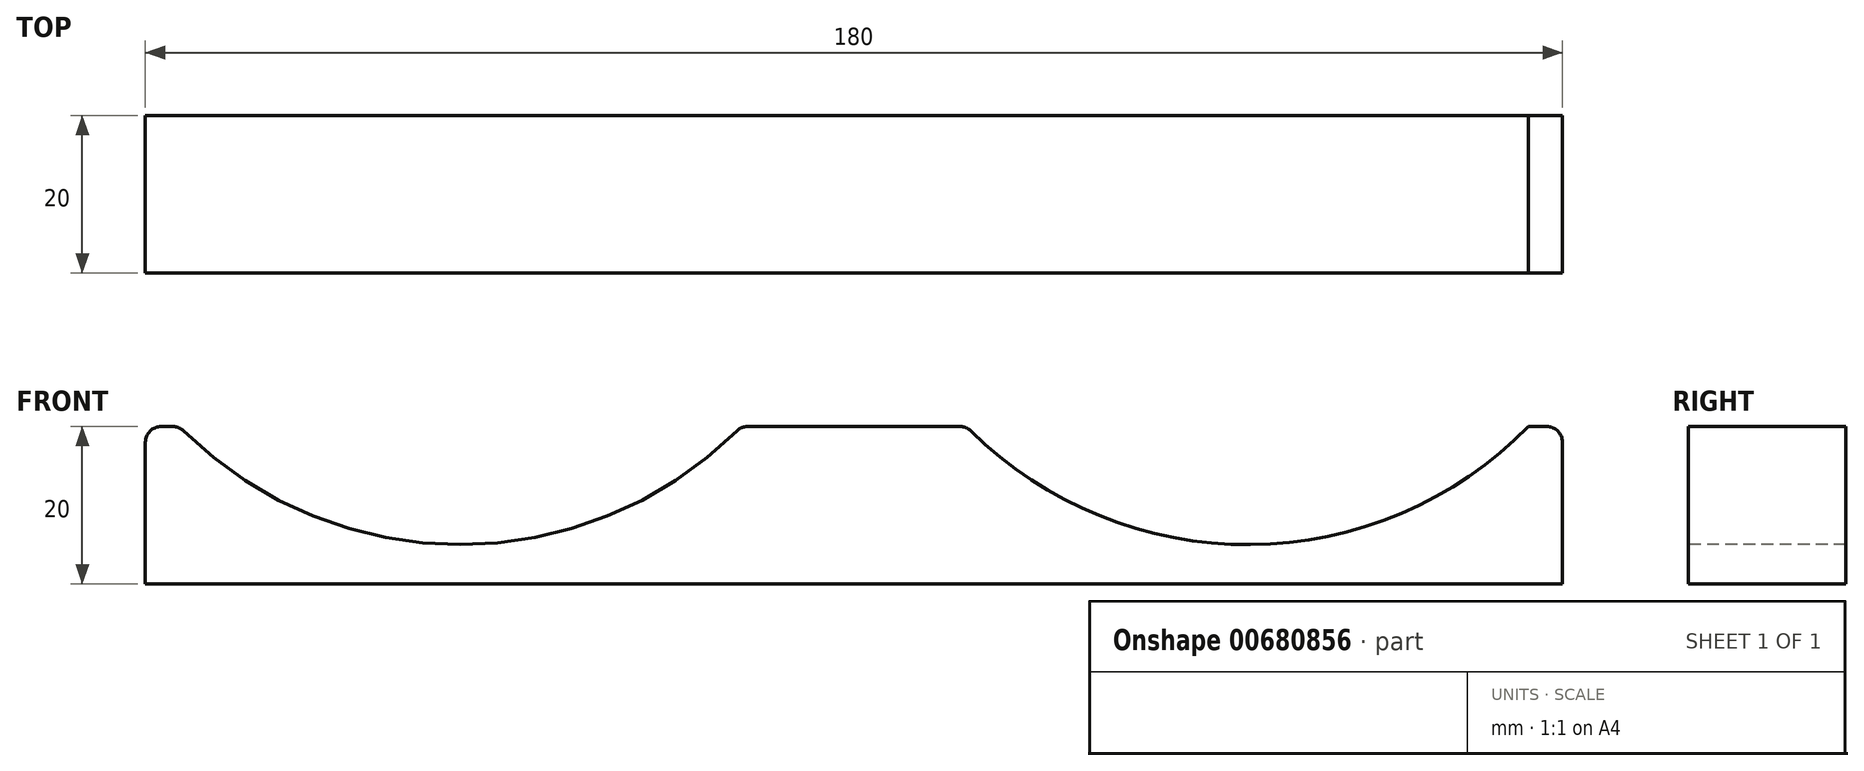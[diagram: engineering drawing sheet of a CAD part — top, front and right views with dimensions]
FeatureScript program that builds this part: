
annotation { "Feature Type Name" : "Feature", "Feature Type Description" : "" }
export const myFeature = defineFeature(function(context is Context, id is Id, definition is map)
    precondition{}
    {
        {
            var Q0;
            Q0=qCreatedBy(makeId("Front.planeOp"),FACE);
            var sketch = newSketch(context, id + "F0", { "sketchPlane" : qUnion([Q0])});
            skLineSegment(sketch, "E0.bottom", {"start": v(0, 0) * mm, "end": v(180, 0) * mm});
            skLineSegment(sketch, "E0.top", {"start": v(0, 20) * mm, "end": v(180, 20) * mm});
            skLineSegment(sketch, "E0.left", {"start": v(0, 0) * mm, "end": v(0, 20) * mm});
            skLineSegment(sketch, "E0.right", {"start": v(180, 0) * mm, "end": v(180, 20) * mm});
            skSolve(sketch);
        }
        {
            var Q0;
            Q0 = qSketchRegion(id + "F0", true);
            extrude(context, id + "F1", {"entities" : qUnion([Q0]), "oppositeDirection" : true, "depth" : 20 * mm, "offsetDistance" : 25 * mm});
        }
        {
            var Q0;
            Q0=makeQuery(id+"F1.opExtrude","CAP_FACE",FACE,{"disambiguationData":[OSD([sQuery(id+"F0.wireOp",EDGE,"E0.bottom"),sQuery(id+"F0.wireOp",EDGE,"E0.top"),sQuery(id+"F0.wireOp",EDGE,"E0.left"),sQuery(id+"F0.wireOp",EDGE,"E0.right")])],"isStart":true});
            var sketch = newSketch(context, id + "F2", { "sketchPlane" : qUnion([Q0])});
            skLineSegment(sketch, "E1", {"start": v(0, 0) * mm, "end": v(40, 0) * mm, "construction": true});
            skLineSegment(sketch, "E2", {"start": v(40, 0) * mm, "end": v(40, 55) * mm, "construction": true});
            skCircle(sketch, "E3", {"center": v(40, 55) * mm, "radius": 50 * mm});
            skLineSegment(sketch, "E4", {"start": v(40, 55) * mm, "end": v(140, 55) * mm, "construction": true});
            skCircle(sketch, "E5", {"center": v(140, 55) * mm, "radius": 50 * mm});
            skSolve(sketch);
        }
        {
            var Q0;
            {var subQ0=sQuery(id+"F2.wireOp",EDGE,"E3");var subQ1=makeQuery(id+"F1.opExtrude","CAP_EDGE",EDGE,{"disambiguationData":[OSD([sQuery(id+"F0.wireOp",EDGE,"E0.top")])],"isStart":true});var subQ2=makeQuery(id+"F2.imprint","INTERSECT",VERTEX,{"disambiguationData":[OD(0.0)],"derivedFrom":[subQ1,subQ0]});Q0=makeQuery(id+"F2.imprint","IMPRINT",FACE,{"disambiguationData":[TD([[makeQuery(id+"F2.imprint","IMPRINT",EDGE,{"disambiguationData":[TD([[subQ2,-1.0]])],"derivedFrom":subQ0}),1.0]])]});}
            var Q1;
            {var subQ0=sQuery(id+"F2.wireOp",EDGE,"E5");var subQ1=makeQuery(id+"F1.opExtrude","CAP_EDGE",EDGE,{"disambiguationData":[OSD([sQuery(id+"F0.wireOp",EDGE,"E0.top")])],"isStart":true});var subQ2=makeQuery(id+"F2.imprint","INTERSECT",VERTEX,{"disambiguationData":[OD(0.0)],"derivedFrom":[subQ1,subQ0]});Q1=makeQuery(id+"F2.imprint","IMPRINT",FACE,{"disambiguationData":[TD([[makeQuery(id+"F2.imprint","IMPRINT",EDGE,{"disambiguationData":[TD([[subQ2,1.0]])],"derivedFrom":subQ0}),1.0]])]});}
            extrude(context, id + "F3", {"entities" : qUnion([Q0, Q1]), "operationType" : NewBodyOperationType.REMOVE, "oppositeDirection" : true, "depth" : 25 * mm, "offsetDistance" : 25 * mm});
        }
        {
            var Q0;
            Q0=makeQuery(id+"F1.opExtrude","SWEPT_EDGE",EDGE,{"disambiguationData":[OSD([sQuery(id+"F0.wireOp",EDGE,"E0.top"),sQuery(id+"F0.wireOp",EDGE,"E0.left")])]});
            var Q1;
            {var subQ0=sQuery(id+"F2.wireOp",EDGE,"E3");var subQ1=sQuery(id+"F0.wireOp",EDGE,"E0.top");Q1=makeQuery(id+"F3.boolean.opBoolean","COPY",EDGE,{"derivedFrom":makeQuery(id+"F3.opExtrude","SWEPT_EDGE",EDGE,{"disambiguationData":[OSD([subQ1,subQ0]),TDD([makeQuery(id+"F2.imprint","INTERSECT",VERTEX,{"disambiguationData":[OD(0.0)],"derivedFrom":[makeQuery(id+"F1.opExtrude","CAP_EDGE",EDGE,{"disambiguationData":[OSD([subQ1])],"isStart":true}),subQ0]})])]})});}
            var Q2;
            {var subQ0=sQuery(id+"F2.wireOp",EDGE,"E3");var subQ1=sQuery(id+"F0.wireOp",EDGE,"E0.top");Q2=makeQuery(id+"F3.boolean.opBoolean","COPY",EDGE,{"derivedFrom":makeQuery(id+"F3.opExtrude","SWEPT_EDGE",EDGE,{"disambiguationData":[OSD([subQ1,subQ0]),TDD([makeQuery(id+"F2.imprint","INTERSECT",VERTEX,{"disambiguationData":[OD(1.0)],"derivedFrom":[makeQuery(id+"F1.opExtrude","CAP_EDGE",EDGE,{"disambiguationData":[OSD([subQ1])],"isStart":true}),subQ0]})])]})});}
            var Q3;
            {var subQ0=sQuery(id+"F2.wireOp",EDGE,"E5");var subQ1=sQuery(id+"F0.wireOp",EDGE,"E0.top");Q3=makeQuery(id+"F3.boolean.opBoolean","COPY",EDGE,{"derivedFrom":makeQuery(id+"F3.opExtrude","SWEPT_EDGE",EDGE,{"disambiguationData":[OSD([subQ1,subQ0]),TDD([makeQuery(id+"F2.imprint","INTERSECT",VERTEX,{"disambiguationData":[OD(1.0)],"derivedFrom":[makeQuery(id+"F1.opExtrude","CAP_EDGE",EDGE,{"disambiguationData":[OSD([subQ1])],"isStart":true}),subQ0]})])]})});}
            var Q4;
            {var subQ0=sQuery(id+"F2.wireOp",EDGE,"E5");var subQ1=sQuery(id+"F0.wireOp",EDGE,"E0.top");Q4=makeQuery(id+"F3.boolean.opBoolean","COPY",EDGE,{"derivedFrom":makeQuery(id+"F3.opExtrude","SWEPT_EDGE",EDGE,{"disambiguationData":[OSD([subQ1,subQ0]),TDD([makeQuery(id+"F2.imprint","INTERSECT",VERTEX,{"disambiguationData":[OD(0.0)],"derivedFrom":[makeQuery(id+"F1.opExtrude","CAP_EDGE",EDGE,{"disambiguationData":[OSD([subQ1])],"isStart":true}),subQ0]})])]})});}
            var Q5;
            Q5=makeQuery(id+"F1.opExtrude","SWEPT_EDGE",EDGE,{"disambiguationData":[OSD([sQuery(id+"F0.wireOp",EDGE,"E0.top"),sQuery(id+"F0.wireOp",EDGE,"E0.right")])]});
            fillet(context, id + "F4", {"entities" : qUnion([Q0, Q1, Q2, Q3, Q4, Q5]), "radius" : 2 * mm, "tangentPropagation" : true, "allowEdgeOverflow" : false});
        }
    });
